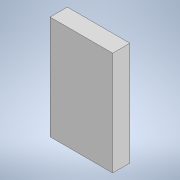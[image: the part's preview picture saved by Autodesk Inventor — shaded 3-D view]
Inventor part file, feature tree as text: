
AUTODESK INVENTOR PART (.ipt)
format: ipt  version: 2022 (Build 260153000, 153)  size: 150,016 bytes
history: native  units: mm
features: extrude x1, sketch x1
ambient origin geometry x8: Origin, YZ Plane, XZ Plane, XY Plane, X Axis, Y Axis, Z Axis, Center Point
bodies: Body1 (feature_tree)
feature tree (2):
  extrude  "Extrusion7"  Depth=67.7mm
  sketch  "Sketch4"  dims[d31=34.456mm d103=67.7mm d104=18.7mm d105=112.2mm d106=0.0mm]
